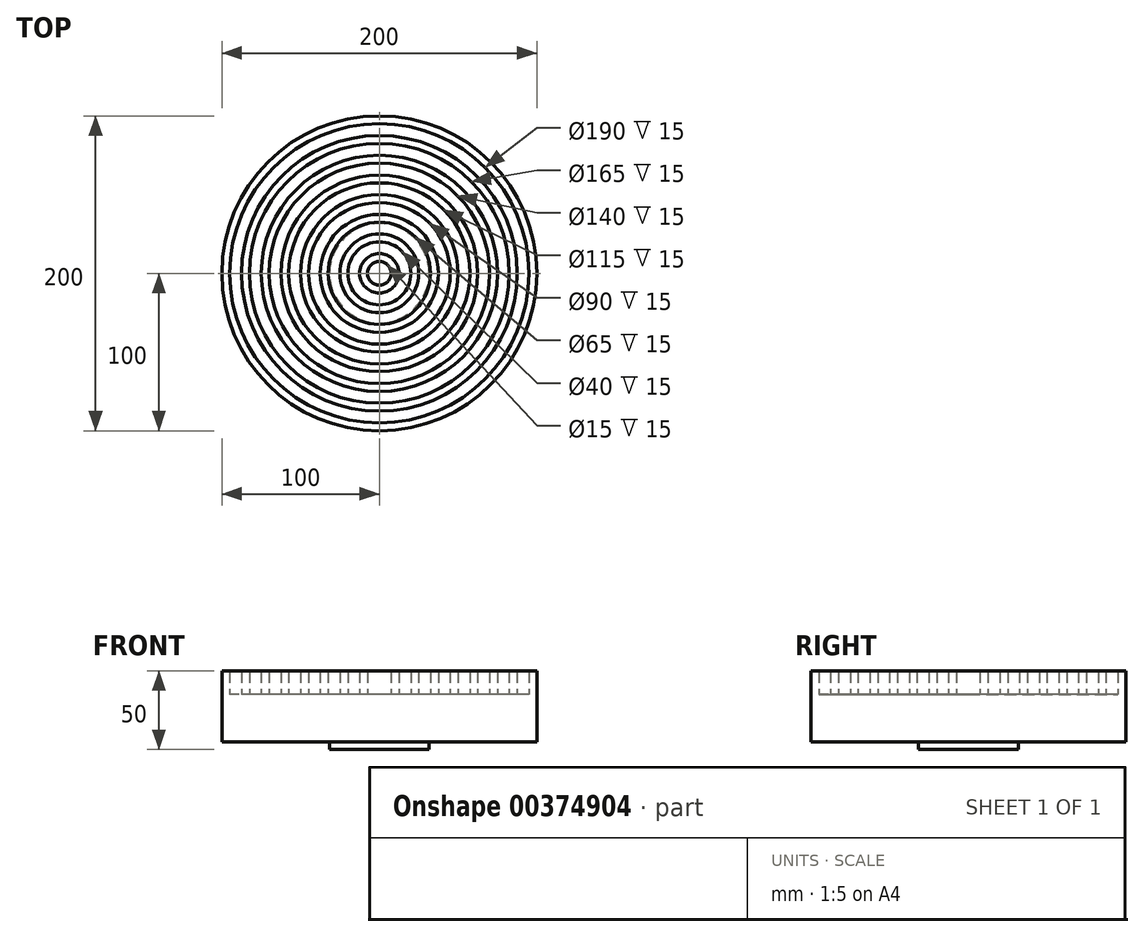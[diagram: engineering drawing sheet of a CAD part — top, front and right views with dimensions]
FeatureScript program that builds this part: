
annotation { "Feature Type Name" : "Feature", "Feature Type Description" : "" }
export const myFeature = defineFeature(function(context is Context, id is Id, definition is map)
    precondition{}
    {
        {
            var Q0;
            Q0=qCreatedBy(makeId("Top.planeOp"),FACE);
            var sketch = newSketch(context, id + "F0", { "sketchPlane" : qUnion([Q0])});
            skCircle(sketch, "E0", {"center": v(0, 0) * mm, "radius": 100 * mm});
            skSolve(sketch);
        }
        {
            var Q0;
            Q0=makeQuery(id+"F0.imprint","IMPRINT",FACE,{"disambiguationData":[TD([[makeQuery(id+"F0.imprint","IMPRINT",EDGE,{"derivedFrom":sQuery(id+"F0.wireOp",EDGE,"E0")}),1.0]])]});
            extrude(context, id + "F1", {"entities" : qUnion([Q0]), "depth" : 5 * mm, "hasSecondDirection" : true, "secondDirectionOppositeDirection" : true, "secondDirectionDepth" : 25 * mm});
        }
        {
            var Q0;
            Q0=makeQuery(id+"F1.opExtrude","CAP_FACE",FACE,{"disambiguationData":[OSD([sQuery(id+"F0.wireOp",EDGE,"E0")])],"isStart":false});
            var sketch = newSketch(context, id + "F2", { "sketchPlane" : qUnion([Q0])});
            skCircle(sketch, "E1", {"center": v(0, 0) * mm, "radius": 95 * mm});
            skCircle(sketch, "E2", {"center": v(0, 0) * mm, "radius": 87.5 * mm});
            skCircle(sketch, "E3", {"center": v(0, 0) * mm, "radius": 82.5 * mm});
            skCircle(sketch, "E4", {"center": v(0, 0) * mm, "radius": 75 * mm});
            skCircle(sketch, "E5", {"center": v(0, 0) * mm, "radius": 70 * mm});
            skCircle(sketch, "E6", {"center": v(0, 0) * mm, "radius": 62.5 * mm});
            skCircle(sketch, "E7", {"center": v(0, 0) * mm, "radius": 57.5 * mm});
            skCircle(sketch, "E8", {"center": v(0, 0) * mm, "radius": 50 * mm});
            skCircle(sketch, "E9", {"center": v(0, 0) * mm, "radius": 45 * mm});
            skCircle(sketch, "E10", {"center": v(0, 0) * mm, "radius": 37.5 * mm});
            skCircle(sketch, "E11", {"center": v(0, 0) * mm, "radius": 32.5 * mm});
            skCircle(sketch, "E12", {"center": v(0, 0) * mm, "radius": 25 * mm});
            skCircle(sketch, "E13", {"center": v(0, 0) * mm, "radius": 20 * mm});
            skCircle(sketch, "E14", {"center": v(0, 0) * mm, "radius": 12.5 * mm});
            skCircle(sketch, "E15", {"center": v(0, 0) * mm, "radius": 7.5 * mm});
            skSolve(sketch);
        }
        {
            var Q0;
            Q0=makeQuery(id+"F2.imprint","IMPRINT",FACE,{"disambiguationData":[TD([[makeQuery(id+"F2.imprint","IMPRINT",EDGE,{"derivedFrom":sQuery(id+"F2.wireOp",EDGE,"E1")}),-1.0]])]});
            var Q1;
            Q1=makeQuery(id+"F2.imprint","IMPRINT",FACE,{"disambiguationData":[TD([[makeQuery(id+"F2.imprint","IMPRINT",EDGE,{"derivedFrom":sQuery(id+"F2.wireOp",EDGE,"E2")}),1.0]])]});
            var Q2;
            Q2=makeQuery(id+"F2.imprint","IMPRINT",FACE,{"disambiguationData":[TD([[makeQuery(id+"F2.imprint","IMPRINT",EDGE,{"derivedFrom":sQuery(id+"F2.wireOp",EDGE,"E4")}),1.0]])]});
            var Q3;
            Q3=makeQuery(id+"F2.imprint","IMPRINT",FACE,{"disambiguationData":[TD([[makeQuery(id+"F2.imprint","IMPRINT",EDGE,{"derivedFrom":sQuery(id+"F2.wireOp",EDGE,"E6")}),1.0]])]});
            var Q4;
            Q4=makeQuery(id+"F2.imprint","IMPRINT",FACE,{"disambiguationData":[TD([[makeQuery(id+"F2.imprint","IMPRINT",EDGE,{"derivedFrom":sQuery(id+"F2.wireOp",EDGE,"E8")}),1.0]])]});
            var Q5;
            Q5=makeQuery(id+"F2.imprint","IMPRINT",FACE,{"disambiguationData":[TD([[makeQuery(id+"F2.imprint","IMPRINT",EDGE,{"derivedFrom":sQuery(id+"F2.wireOp",EDGE,"E10")}),1.0]])]});
            var Q6;
            Q6=makeQuery(id+"F2.imprint","IMPRINT",FACE,{"disambiguationData":[TD([[makeQuery(id+"F2.imprint","IMPRINT",EDGE,{"derivedFrom":sQuery(id+"F2.wireOp",EDGE,"E12")}),1.0]])]});
            var Q7;
            Q7=makeQuery(id+"F2.imprint","IMPRINT",FACE,{"disambiguationData":[TD([[makeQuery(id+"F2.imprint","IMPRINT",EDGE,{"derivedFrom":sQuery(id+"F2.wireOp",EDGE,"E14")}),1.0]])]});
            extrude(context, id + "F3", {"entities" : qUnion([Q0, Q1, Q2, Q3, Q4, Q5, Q6, Q7]), "operationType" : NewBodyOperationType.ADD, "depth" : 15 * mm});
        }
        {
            var Q0;
            Q0=makeQuery(id+"F1.opExtrude","CAP_FACE",FACE,{"disambiguationData":[OSD([sQuery(id+"F0.wireOp",EDGE,"E0")])],"isStart":true});
            var sketch = newSketch(context, id + "F4", { "sketchPlane" : qUnion([Q0])});
            skCircle(sketch, "E16", {"center": v(0, 0) * mm, "radius": 31.66 * mm});
            skSolve(sketch);
        }
        {
            var Q0;
            Q0=makeQuery(id+"F4.imprint","IMPRINT",FACE,{"disambiguationData":[TD([[makeQuery(id+"F4.imprint","IMPRINT",EDGE,{"derivedFrom":sQuery(id+"F4.wireOp",EDGE,"E16")}),1.0]])]});
            extrude(context, id + "F5", {"entities" : qUnion([Q0]), "operationType" : NewBodyOperationType.ADD, "depth" : 5 * mm});
        }
    });
